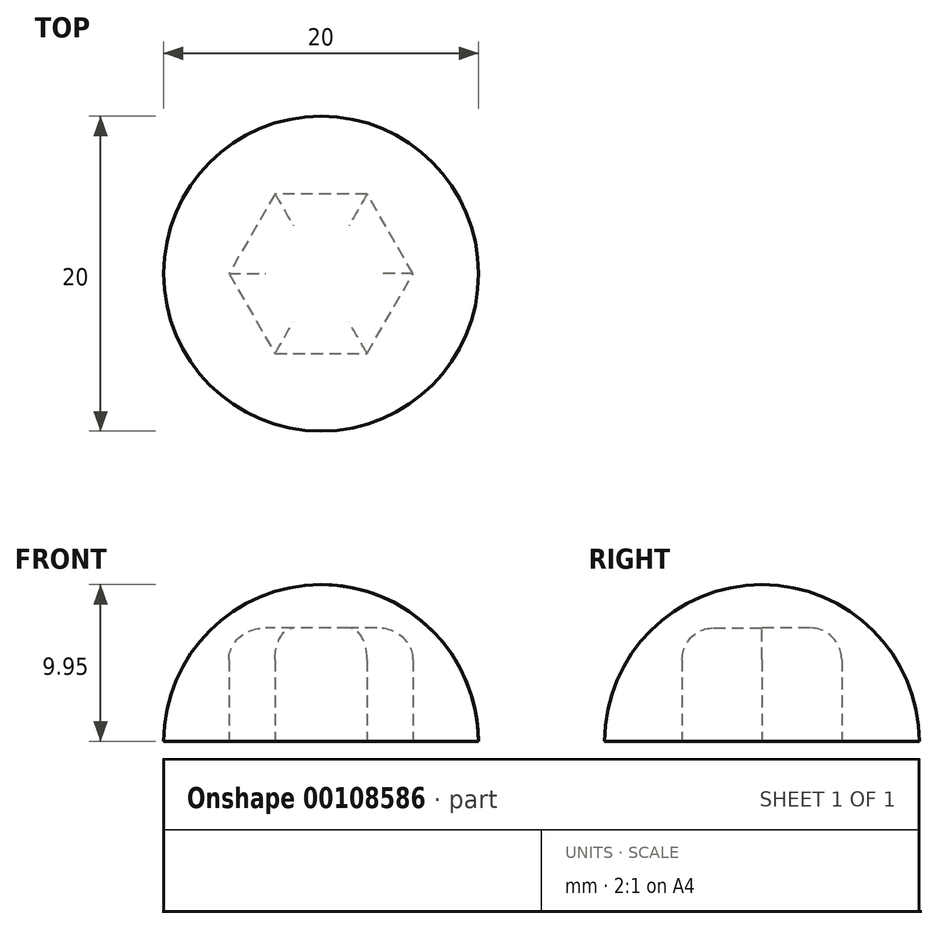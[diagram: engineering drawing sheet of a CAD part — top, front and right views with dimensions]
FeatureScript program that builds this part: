
annotation { "Feature Type Name" : "Feature", "Feature Type Description" : "" }
export const myFeature = defineFeature(function(context is Context, id is Id, definition is map)
    precondition{}
    {
        {
            assignVariable(context, id + "F0", {"name" : "H", "anyValue" : 6.2});
        }
        {
            var Q0;
            Q0=qCreatedBy(makeId("Front.planeOp"),FACE);
            var sketch = newSketch(context, id + "F1", { "sketchPlane" : qUnion([Q0])});
            skArc(sketch, "E0", {"start": v(10, 0) * mm, "mid": v(7.05, 7.04) * mm, "end": v(0, 9.95) * mm, "construction": true});
            skLineSegment(sketch, "E1", {"start": v(-10, 0) * mm, "end": v(0, 0) * mm});
            skLineSegment(sketch, "E2", {"start": v(0, 0) * mm, "end": v(0, 9.95) * mm});
            skLineSegment(sketch, "E3", {"start": v(-5.65, 0) * mm, "end": v(-5.65, 8.2) * mm, "construction": true});
            skArc(sketch, "E4", {"start": v(0, 9.95) * mm, "mid": v(-7.05, 7.04) * mm, "end": v(-10, 0) * mm});
            skLineSegment(sketch, "E5", {"start": v(0, 0) * mm, "end": v(10, 0) * mm, "construction": true});
            skSolve(sketch);
        }
        {
            var Q0;
            Q0=qSketchRegion(id+"F1",true);
            var Q1;
            Q1=sQuery(id+"F1.wireOp",EDGE,"E2");
            revolve(context, id + "F2", {"entities" : qUnion([Q0]), "axis" : qUnion([Q1]), "revolveType" : RevolveType.FULL});
        }
        {
            var Q0;
            Q0=makeQuery(id+"F2.opRevolve","SWEPT_FACE",FACE,{"disambiguationData":[OSD([sQuery(id+"F1.wireOp",EDGE,"E1")])]});
            var sketch = newSketch(context, id + "F3", { "sketchPlane" : qUnion([Q0])});
            skCircle(sketch, "E6.cCircle", {"center": v(0, 0) * mm, "radius": 5.85 * mm, "construction": true});
            skLineSegment(sketch, "E6.0", {"start": v(-2.93, 5.07) * mm, "end": v(2.92, 5.07) * mm});
            skLineSegment(sketch, "E6.1", {"start": v(2.92, 5.07) * mm, "end": v(5.85, 0) * mm});
            skLineSegment(sketch, "E6.2", {"start": v(5.85, 0) * mm, "end": v(2.93, -5.07) * mm});
            skLineSegment(sketch, "E6.3", {"start": v(2.93, -5.07) * mm, "end": v(-2.92, -5.07) * mm});
            skLineSegment(sketch, "E6.4", {"start": v(-2.92, -5.07) * mm, "end": v(-5.85, 0) * mm});
            skLineSegment(sketch, "E6.5", {"start": v(-5.85, 0) * mm, "end": v(-2.93, 5.07) * mm});
            skSolve(sketch);
        }
        {
            var Q0;
            Q0=makeQuery(id+"F3.imprint","IMPRINT",FACE,{"disambiguationData":[TD([[makeQuery(id+"F3.imprint","IMPRINT",EDGE,{"derivedFrom":sQuery(id+"F3.wireOp",EDGE,"E6.0")}),-1.0]])]});
            extrude(context, id + "F4", {"entities" : qUnion([Q0]), "operationType" : NewBodyOperationType.REMOVE, "oppositeDirection" : true, "depth" : (getVariable(context, 'H') + 1) * mm});
        }
        {
            var Q0;
            Q0=makeQuery(id+"F4.boolean.opBoolean","COPY",EDGE,{"derivedFrom":makeQuery(id+"F4.opExtrude","CAP_EDGE",EDGE,{"disambiguationData":[OSD([sQuery(id+"F3.wireOp",EDGE,"E6.0")])],"isStart":false})});
            var Q1;
            Q1=makeQuery(id+"F4.boolean.opBoolean","COPY",EDGE,{"derivedFrom":makeQuery(id+"F4.opExtrude","CAP_EDGE",EDGE,{"disambiguationData":[OSD([sQuery(id+"F3.wireOp",EDGE,"E6.5")])],"isStart":false})});
            var Q2;
            Q2=makeQuery(id+"F4.boolean.opBoolean","COPY",EDGE,{"derivedFrom":makeQuery(id+"F4.opExtrude","CAP_EDGE",EDGE,{"disambiguationData":[OSD([sQuery(id+"F3.wireOp",EDGE,"E6.1")])],"isStart":false})});
            var Q3;
            Q3=makeQuery(id+"F4.boolean.opBoolean","COPY",EDGE,{"derivedFrom":makeQuery(id+"F4.opExtrude","CAP_EDGE",EDGE,{"disambiguationData":[OSD([sQuery(id+"F3.wireOp",EDGE,"E6.2")])],"isStart":false})});
            var Q4;
            Q4=makeQuery(id+"F4.boolean.opBoolean","COPY",EDGE,{"derivedFrom":makeQuery(id+"F4.opExtrude","CAP_EDGE",EDGE,{"disambiguationData":[OSD([sQuery(id+"F3.wireOp",EDGE,"E6.4")])],"isStart":false})});
            var Q5;
            Q5=makeQuery(id+"F4.boolean.opBoolean","COPY",EDGE,{"derivedFrom":makeQuery(id+"F4.opExtrude","CAP_EDGE",EDGE,{"disambiguationData":[OSD([sQuery(id+"F3.wireOp",EDGE,"E6.3")])],"isStart":false})});
            fillet(context, id + "F5", {"entities" : qUnion([Q0, Q1, Q2, Q3, Q4, Q5]), "radius" : 2 * mm, "tangentPropagation" : true, "allowEdgeOverflow" : false});
        }
    });
